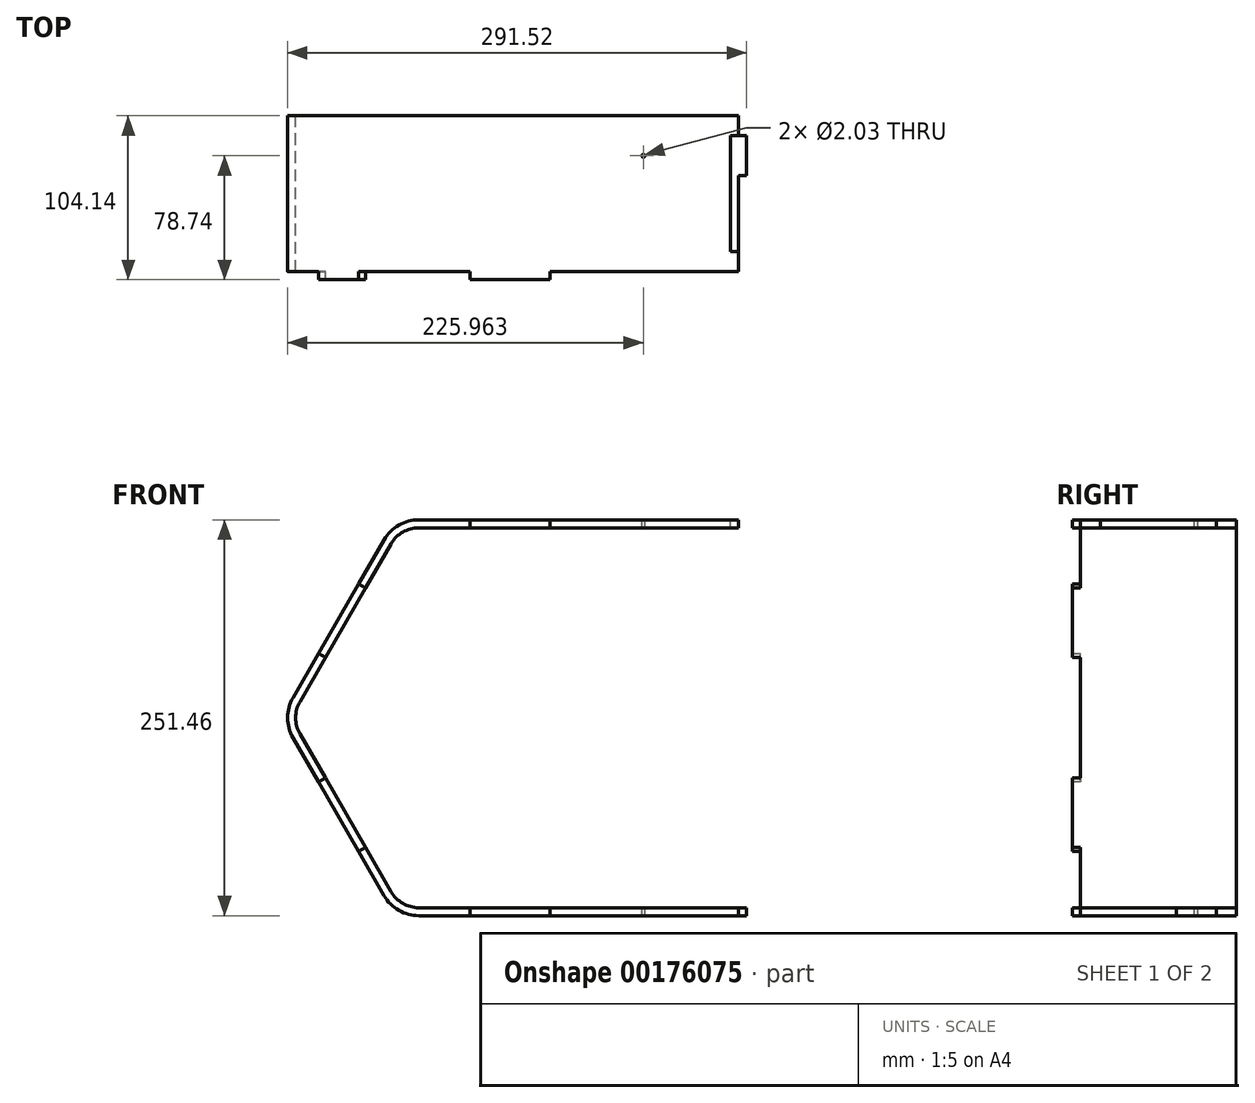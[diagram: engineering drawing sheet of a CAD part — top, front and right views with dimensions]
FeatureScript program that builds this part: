
annotation { "Feature Type Name" : "Feature", "Feature Type Description" : "" }
export const myFeature = defineFeature(function(context is Context, id is Id, definition is map)
    precondition{}
    {
        {
            var Q0;
            Q0=qCreatedBy(makeId("Front.planeOp"),FACE);
            var sketch = newSketch(context, id + "F0", { "sketchPlane" : qUnion([Q0])});
            skLineSegment(sketch, "E0", {"start": v(0, 0) * mm, "end": v(-203.11, 0) * mm});
            skLineSegment(sketch, "E1", {"start": v(-225.11, 12.7) * mm, "end": v(-283.03, 113.03) * mm});
            skLineSegment(sketch, "E2", {"start": v(-283.03, 138.43) * mm, "end": v(-225.11, 238.76) * mm});
            skLineSegment(sketch, "E3", {"start": v(-203.11, 251.46) * mm, "end": v(0, 251.46) * mm});
            skPoint(sketch, "E4.visualSharp", {"position": v(-217.78, 251.46) * mm});
            skArc(sketch, "E4.filletArc", {"start": v(-203.11, 251.46) * mm, "mid": v(-215.81, 248.06) * mm, "end": v(-225.11, 238.76) * mm});
            skPoint(sketch, "E5.visualSharp", {"position": v(-290.37, 125.73) * mm});
            skArc(sketch, "E5.filletArc", {"start": v(-283.03, 138.43) * mm, "mid": v(-286.44, 125.73) * mm, "end": v(-283.03, 113.03) * mm});
            skPoint(sketch, "E6.visualSharp", {"position": v(-217.78, 0) * mm});
            skArc(sketch, "E6.filletArc", {"start": v(-225.11, 12.7) * mm, "mid": v(-215.81, 3.4) * mm, "end": v(-203.11, 0) * mm});
            skLineSegment(sketch, "E7.0", {"start": v(-203.11, 246.38) * mm, "end": v(0, 246.38) * mm});
            skArc(sketch, "E7.1", {"start": v(-203.11, 246.38) * mm, "mid": v(-213.27, 243.66) * mm, "end": v(-220.71, 236.22) * mm});
            skLineSegment(sketch, "E7.2", {"start": v(-278.63, 135.89) * mm, "end": v(-220.71, 236.22) * mm});
            skLineSegment(sketch, "E7.3", {"start": v(0, 5.08) * mm, "end": v(-203.11, 5.08) * mm});
            skArc(sketch, "E7.4", {"start": v(-220.71, 15.24) * mm, "mid": v(-213.27, 7.8) * mm, "end": v(-203.11, 5.08) * mm});
            skLineSegment(sketch, "E7.5", {"start": v(-220.71, 15.24) * mm, "end": v(-278.63, 115.57) * mm});
            skArc(sketch, "E7.6", {"start": v(-278.63, 135.89) * mm, "mid": v(-281.36, 125.73) * mm, "end": v(-278.63, 115.57) * mm});
            skLineSegment(sketch, "E8", {"start": v(0, 246.38) * mm, "end": v(0, 251.46) * mm});
            skLineSegment(sketch, "E9", {"start": v(0, 5.08) * mm, "end": v(0, 0) * mm});
            skSolve(sketch);
        }
        {
            var Q0;
            Q0 = qSketchRegion(id + "F0", true);
            extrude(context, id + "F1", {"entities" : qUnion([Q0]), "depth" : 99.06 * mm});
        }
        {
            var Q0;
            Q0=makeQuery(id+"F1.opExtrude","SWEPT_FACE",FACE,{"disambiguationData":[OSD([sQuery(id+"F0.wireOp",EDGE,"E3")])]});
            var sketch = newSketch(context, id + "F2", { "sketchPlane" : qUnion([Q0])});
            skLineSegment(sketch, "E10.bottom", {"start": v(-170.59, -99.06) * mm, "end": v(-119.79, -99.06) * mm});
            skLineSegment(sketch, "E10.top", {"start": v(-170.59, -104.14) * mm, "end": v(-119.79, -104.14) * mm});
            skLineSegment(sketch, "E10.left", {"start": v(-119.79, -99.06) * mm, "end": v(-119.79, -104.14) * mm});
            skLineSegment(sketch, "E10.right", {"start": v(-170.59, -99.06) * mm, "end": v(-170.59, -104.14) * mm});
            skPoint(sketch, "E11", {"position": v(-145.19, -104.14) * mm});
            skSolve(sketch);
        }
        {
            var Q0;
            Q0=makeQuery(id+"F1.opExtrude","CAP_FACE",FACE,{"disambiguationData":[OSD([sQuery(id+"F0.wireOp",EDGE,"E0"),sQuery(id+"F0.wireOp",EDGE,"E1"),sQuery(id+"F0.wireOp",EDGE,"E2"),sQuery(id+"F0.wireOp",EDGE,"E3"),sQuery(id+"F0.wireOp",EDGE,"E4.filletArc"),sQuery(id+"F0.wireOp",EDGE,"E5.filletArc"),sQuery(id+"F0.wireOp",EDGE,"E6.filletArc"),sQuery(id+"F0.wireOp",EDGE,"E7.0"),sQuery(id+"F0.wireOp",EDGE,"E7.1"),sQuery(id+"F0.wireOp",EDGE,"E7.2"),sQuery(id+"F0.wireOp",EDGE,"E7.3"),sQuery(id+"F0.wireOp",EDGE,"E7.4"),sQuery(id+"F0.wireOp",EDGE,"E7.5"),sQuery(id+"F0.wireOp",EDGE,"E7.6"),sQuery(id+"F0.wireOp",EDGE,"E8"),sQuery(id+"F0.wireOp",EDGE,"E9")])],"isStart":false});
            var Q1;
            Q1=makeQuery(id+"F1.opExtrude","CAP_FACE",FACE,{"disambiguationData":[OSD([sQuery(id+"F0.wireOp",EDGE,"E0"),sQuery(id+"F0.wireOp",EDGE,"E1"),sQuery(id+"F0.wireOp",EDGE,"E2"),sQuery(id+"F0.wireOp",EDGE,"E3"),sQuery(id+"F0.wireOp",EDGE,"E4.filletArc"),sQuery(id+"F0.wireOp",EDGE,"E5.filletArc"),sQuery(id+"F0.wireOp",EDGE,"E6.filletArc"),sQuery(id+"F0.wireOp",EDGE,"E7.0"),sQuery(id+"F0.wireOp",EDGE,"E7.1"),sQuery(id+"F0.wireOp",EDGE,"E7.2"),sQuery(id+"F0.wireOp",EDGE,"E7.3"),sQuery(id+"F0.wireOp",EDGE,"E7.4"),sQuery(id+"F0.wireOp",EDGE,"E7.5"),sQuery(id+"F0.wireOp",EDGE,"E7.6"),sQuery(id+"F0.wireOp",EDGE,"E8"),sQuery(id+"F0.wireOp",EDGE,"E9")])],"isStart":true});
            cPlane(context, id + "F3", {"entities" : qUnion([Q0, Q1]), "cplaneType" : CPlaneType.MID_PLANE, "offset" : 25.4 * mm, "width" : 152.4 * mm, "height" : 152.4 * mm});
        }
        {
            var Q0;
            Q0=makeQuery(id+"F2.imprint","IMPRINT",FACE,{"disambiguationData":[TD([[makeQuery(id+"F2.imprint","IMPRINT",EDGE,{"derivedFrom":sQuery(id+"F2.wireOp",EDGE,"E10.bottom")}),-1.0]])]});
            var Q1;
            Q1=makeQuery(id+"F1.opExtrude","SWEPT_FACE",FACE,{"disambiguationData":[OSD([sQuery(id+"F0.wireOp",EDGE,"E7.0")])]});
            extrude(context, id + "F4", {"entities" : qUnion([Q0]), "operationType" : NewBodyOperationType.ADD, "endBound" : BoundingType.UP_TO_SURFACE, "oppositeDirection" : true, "endBoundEntityFace" : qUnion([Q1]), "depth" : 25.4 * mm});
        }
        {
            var Q0;
            Q0=makeQuery(id+"F1.opExtrude","SWEPT_FACE",FACE,{"disambiguationData":[OSD([sQuery(id+"F0.wireOp",EDGE,"E2")])]});
            var sketch = newSketch(context, id + "F5", { "sketchPlane" : qUnion([Q0])});
            skLineSegment(sketch, "E12.bottom", {"start": v(104.14, 61.7) * mm, "end": v(99.06, 61.7) * mm});
            skLineSegment(sketch, "E12.top", {"start": v(104.14, 10.9) * mm, "end": v(99.06, 10.9) * mm});
            skLineSegment(sketch, "E12.left", {"start": v(104.14, 61.7) * mm, "end": v(104.14, 10.9) * mm});
            skLineSegment(sketch, "E12.right", {"start": v(99.06, 61.7) * mm, "end": v(99.06, 10.9) * mm});
            skPoint(sketch, "E13", {"position": v(99.06, 36.3) * mm});
            skPoint(sketch, "E14", {"position": v(104.14, 36.3) * mm});
            skSolve(sketch);
        }
        {
            var Q0;
            Q0 = qSketchRegion(id + "F5", true);
            var Q1;
            Q1=makeQuery(id+"F1.opExtrude","SWEPT_FACE",FACE,{"disambiguationData":[OSD([sQuery(id+"F0.wireOp",EDGE,"E7.2")])]});
            extrude(context, id + "F6", {"entities" : qUnion([Q0]), "operationType" : NewBodyOperationType.ADD, "endBound" : BoundingType.UP_TO_SURFACE, "oppositeDirection" : true, "endBoundEntityFace" : qUnion([Q1]), "depth" : 25.4 * mm});
        }
        {
            var Q0;
            Q0=makeQuery(id+"F1.opExtrude","SWEPT_FACE",FACE,{"disambiguationData":[OSD([sQuery(id+"F0.wireOp",EDGE,"E1")])]});
            var sketch = newSketch(context, id + "F7", { "sketchPlane" : qUnion([Q0])});
            skPoint(sketch, "E15", {"position": v(99.06, 181.47) * mm});
            skLineSegment(sketch, "E16.bottom", {"start": v(99.06, 206.87) * mm, "end": v(104.14, 206.87) * mm});
            skLineSegment(sketch, "E16.top", {"start": v(99.06, 156.07) * mm, "end": v(104.14, 156.07) * mm});
            skLineSegment(sketch, "E16.left", {"start": v(99.06, 206.87) * mm, "end": v(99.06, 156.07) * mm});
            skLineSegment(sketch, "E16.right", {"start": v(104.14, 206.87) * mm, "end": v(104.14, 156.07) * mm});
            skPoint(sketch, "E17", {"position": v(104.14, 181.47) * mm});
            skSolve(sketch);
        }
        {
            var Q0;
            Q0 = qSketchRegion(id + "F7", true);
            var Q1;
            Q1=makeQuery(id+"F1.opExtrude","SWEPT_FACE",FACE,{"disambiguationData":[OSD([sQuery(id+"F0.wireOp",EDGE,"E7.5")])]});
            extrude(context, id + "F8", {"entities" : qUnion([Q0]), "operationType" : NewBodyOperationType.ADD, "endBound" : BoundingType.UP_TO_SURFACE, "oppositeDirection" : true, "endBoundEntityFace" : qUnion([Q1]), "depth" : 25.4 * mm});
        }
        {
            var Q0;
            Q0=makeQuery(id+"F1.opExtrude","SWEPT_FACE",FACE,{"disambiguationData":[OSD([sQuery(id+"F0.wireOp",EDGE,"E0")])]});
            var sketch = newSketch(context, id + "F9", { "sketchPlane" : qUnion([Q0])});
            skPoint(sketch, "E18", {"position": v(-101.56, 99.06) * mm});
            skLineSegment(sketch, "E19.bottom", {"start": v(-170.59, 99.06) * mm, "end": v(-119.79, 99.06) * mm});
            skLineSegment(sketch, "E19.top", {"start": v(-170.59, 104.14) * mm, "end": v(-119.79, 104.14) * mm});
            skLineSegment(sketch, "E19.left", {"start": v(-170.59, 99.06) * mm, "end": v(-170.59, 104.14) * mm});
            skLineSegment(sketch, "E19.right", {"start": v(-119.79, 99.06) * mm, "end": v(-119.79, 104.14) * mm});
            skPoint(sketch, "E20", {"position": v(-145.19, 104.14) * mm});
            skSolve(sketch);
        }
        {
            var Q0;
            Q0=makeQuery(id+"F9.imprint","IMPRINT",FACE,{"disambiguationData":[TD([[makeQuery(id+"F9.imprint","IMPRINT",EDGE,{"derivedFrom":sQuery(id+"F9.wireOp",EDGE,"E19.bottom")}),-1.0]])]});
            var Q1;
            Q1=makeQuery(id+"F1.opExtrude","SWEPT_FACE",FACE,{"disambiguationData":[OSD([sQuery(id+"F0.wireOp",EDGE,"E7.3")])]});
            extrude(context, id + "F10", {"entities" : qUnion([Q0]), "operationType" : NewBodyOperationType.ADD, "endBound" : BoundingType.UP_TO_SURFACE, "oppositeDirection" : true, "endBoundEntityFace" : qUnion([Q1]), "depth" : 25.4 * mm});
        }
        {
            var Q0;
            {var subQ0=sQuery(id+"F9.wireOp",EDGE,"E19.right");var subQ1=sQuery(id+"F9.wireOp",EDGE,"E19.left");var subQ2=sQuery(id+"F9.wireOp",EDGE,"E19.top");var subQ3=sQuery(id+"F9.wireOp",EDGE,"E19.bottom");Q0=makeQuery(id+"FOcjj00AabnaQMC_1.1.F10.boolean.opBoolean","MERGE",FACE,{"derivedFrom":[makeQuery(id+"F10.boolean.opBoolean","MERGE",FACE,{"derivedFrom":[makeQuery(id+"F1.opExtrude","SWEPT_FACE",FACE,{"disambiguationData":[OSD([sQuery(id+"F0.wireOp",EDGE,"E0")])]}),makeQuery(id+"F10.opExtrude","CAP_FACE",FACE,{"disambiguationData":[OSD([subQ3,subQ2,subQ1,subQ0])],"isStart":true})]}),makeQuery(id+"FOcjj00AabnaQMC_1.1.F10.opExtrude","CAP_FACE",FACE,{"disambiguationData":[OSD([subQ3,subQ2,subQ1,subQ0])],"isStart":true})]});}
            var sketch = newSketch(context, id + "F11", { "sketchPlane" : qUnion([Q0])});
            skLineSegment(sketch, "E21", {"start": v(0, 38.1) * mm, "end": v(5.08, 38.1) * mm});
            skLineSegment(sketch, "E22", {"start": v(5.08, 38.1) * mm, "end": v(5.08, 12.7) * mm});
            skLineSegment(sketch, "E23", {"start": v(5.08, 12.7) * mm, "end": v(0, 12.7) * mm});
            skPoint(sketch, "E24", {"position": v(5.08, 25.4) * mm});
            skSolve(sketch);
        }
        {
            var Q0;
            Q0=makeQuery(id+"F11.imprint","IMPRINT",FACE,{"disambiguationData":[TD([[makeQuery(id+"F11.imprint","IMPRINT",EDGE,{"derivedFrom":sQuery(id+"F11.wireOp",EDGE,"dBCN2MHi-L73X-COiZ-1369-i9UW4HQ0UOL0.bottom")}),-1.0]])]});
            var Q1;
            Q1=makeQuery(id+"F11.imprint","IMPRINT",FACE,{"disambiguationData":[TD([[makeQuery(id+"F11.imprint","IMPRINT",EDGE,{"derivedFrom":sQuery(id+"F11.wireOp",EDGE,"uv0YM2hh-z9AA-CsHQ-nxxI-EjLRfSeFv6UL.bottom")}),1.0]])]});
            var Q2;
            {var subQ0=sQuery(id+"F11.wireOp",EDGE,"E21");Q2=makeQuery(id+"F11.imprint","IMPRINT",FACE,{"disambiguationData":[TD([[makeQuery(id+"F11.imprint","IMPRINT",EDGE,{"derivedFrom":subQ0}),-1.0]])]});}
            var Q3;
            {var subQ0=sQuery(id+"F0.wireOp",EDGE,"E7.3");Q3=makeQuery(id+"FOcjj00AabnaQMC_1.1.F10.boolean.opBoolean","MERGE",FACE,{"derivedFrom":[makeQuery(id+"F10.boolean.opBoolean","MERGE",FACE,{"derivedFrom":[makeQuery(id+"F1.opExtrude","SWEPT_FACE",FACE,{"disambiguationData":[OSD([subQ0])]}),makeQuery(id+"F10.opExtrude","CAP_FACE",FACE,{"disambiguationData":[OSD([subQ0])],"isStart":false})]}),makeQuery(id+"FOcjj00AabnaQMC_1.1.F10.opExtrude","CAP_FACE",FACE,{"disambiguationData":[OSD([subQ0])],"isStart":false})]});}
            extrude(context, id + "F12", {"entities" : qUnion([Q0, Q1, Q2]), "operationType" : NewBodyOperationType.ADD, "endBound" : BoundingType.UP_TO_SURFACE, "oppositeDirection" : true, "endBoundEntityFace" : qUnion([Q3]), "depth" : 25.4 * mm});
        }
        {
            var Q0;
            {var subQ0=sQuery(id+"F2.wireOp",EDGE,"E10.right");var subQ1=sQuery(id+"F2.wireOp",EDGE,"E10.left");var subQ2=sQuery(id+"F2.wireOp",EDGE,"E10.top");var subQ3=sQuery(id+"F2.wireOp",EDGE,"E10.bottom");Q0=makeQuery(id+"FA9yLEBiCmp2qDI_1.1.F4.boolean.opBoolean","MERGE",FACE,{"derivedFrom":[makeQuery(id+"F4.boolean.opBoolean","MERGE",FACE,{"derivedFrom":[makeQuery(id+"F1.opExtrude","SWEPT_FACE",FACE,{"disambiguationData":[OSD([sQuery(id+"F0.wireOp",EDGE,"E3")])]}),makeQuery(id+"F4.opExtrude","CAP_FACE",FACE,{"disambiguationData":[OSD([subQ3,subQ2,subQ1,subQ0])],"isStart":true})]}),makeQuery(id+"FA9yLEBiCmp2qDI_1.1.F4.opExtrude","CAP_FACE",FACE,{"disambiguationData":[OSD([subQ3,subQ2,subQ1,subQ0])],"isStart":true})]});}
            var sketch = newSketch(context, id + "F13", { "sketchPlane" : qUnion([Q0])});
            skLineSegment(sketch, "E25", {"start": v(-5.08, -99.06) * mm, "end": v(-5.08, -86.36) * mm});
            skLineSegment(sketch, "E26", {"start": v(-5.08, -86.36) * mm, "end": v(0, -86.36) * mm});
            skLineSegment(sketch, "E27", {"start": v(0, -12.7) * mm, "end": v(-5.08, -12.7) * mm});
            skLineSegment(sketch, "E28", {"start": v(-5.08, -12.7) * mm, "end": v(-5.08, 0) * mm});
            skLineSegment(sketch, "E29", {"start": v(-5.08, -86.36) * mm, "end": v(-5.08, -12.7) * mm});
            skSolve(sketch);
        }
        {
            var Q0;
            Q0=makeQuery(id+"F13.imprint","IMPRINT",FACE,{"disambiguationData":[TD([[makeQuery(id+"F13.imprint","IMPRINT",EDGE,{"derivedFrom":sQuery(id+"F13.wireOp",EDGE,"I0PWTSSI-DO5l-hUTM-lzc9-wJIb2kJdT08f.bottom")}),1.0]])]});
            var Q1;
            Q1=makeQuery(id+"F13.imprint","IMPRINT",FACE,{"disambiguationData":[TD([[makeQuery(id+"F13.imprint","IMPRINT",EDGE,{"derivedFrom":sQuery(id+"F13.wireOp",EDGE,"Z0djA6Wr-vS1q-zq7I-qstk-N1caMg06y9J0.bottom")}),-1.0]])]});
            var Q2;
            {var subQ0=sQuery(id+"F13.wireOp",EDGE,"E26");Q2=makeQuery(id+"F13.imprint","IMPRINT",FACE,{"disambiguationData":[TD([[makeQuery(id+"F13.imprint","IMPRINT",EDGE,{"derivedFrom":subQ0}),1.0]])]});}
            var Q3;
            {var subQ0=sQuery(id+"F0.wireOp",EDGE,"E7.0");Q3=makeQuery(id+"FA9yLEBiCmp2qDI_1.1.F4.boolean.opBoolean","MERGE",FACE,{"derivedFrom":[makeQuery(id+"F4.boolean.opBoolean","MERGE",FACE,{"derivedFrom":[makeQuery(id+"F1.opExtrude","SWEPT_FACE",FACE,{"disambiguationData":[OSD([subQ0])]}),makeQuery(id+"F4.opExtrude","CAP_FACE",FACE,{"disambiguationData":[OSD([subQ0])],"isStart":false})]}),makeQuery(id+"FA9yLEBiCmp2qDI_1.1.F4.opExtrude","CAP_FACE",FACE,{"disambiguationData":[OSD([subQ0])],"isStart":false})]});}
            extrude(context, id + "F14", {"entities" : qUnion([Q0, Q1, Q2]), "operationType" : NewBodyOperationType.REMOVE, "endBound" : BoundingType.UP_TO_SURFACE, "oppositeDirection" : true, "endBoundEntityFace" : qUnion([Q3]), "depth" : 25.4 * mm});
        }
        {
            var Q0;
            {var subQ0=sQuery(id+"F2.wireOp",EDGE,"E10.right");var subQ1=sQuery(id+"F2.wireOp",EDGE,"E10.left");var subQ2=sQuery(id+"F2.wireOp",EDGE,"E10.top");var subQ3=sQuery(id+"F2.wireOp",EDGE,"E10.bottom");Q0=makeQuery(id+"FA9yLEBiCmp2qDI_1.1.F4.boolean.opBoolean","MERGE",FACE,{"derivedFrom":[makeQuery(id+"F4.boolean.opBoolean","MERGE",FACE,{"derivedFrom":[makeQuery(id+"F1.opExtrude","SWEPT_FACE",FACE,{"disambiguationData":[OSD([sQuery(id+"F0.wireOp",EDGE,"E3")])]}),makeQuery(id+"F4.opExtrude","CAP_FACE",FACE,{"disambiguationData":[OSD([subQ3,subQ2,subQ1,subQ0])],"isStart":true})]}),makeQuery(id+"FA9yLEBiCmp2qDI_1.1.F4.opExtrude","CAP_FACE",FACE,{"disambiguationData":[OSD([subQ3,subQ2,subQ1,subQ0])],"isStart":true})]});}
            var sketch = newSketch(context, id + "F15", { "sketchPlane" : qUnion([Q0])});
            skLineSegment(sketch, "E30.bottom", {"start": v(-63.02, -12.7) * mm, "end": v(-57.94, -12.7) * mm, "construction": true});
            skLineSegment(sketch, "E30.top", {"start": v(-63.02, -38.1) * mm, "end": v(-57.94, -38.1) * mm, "construction": true});
            skLineSegment(sketch, "E30.left", {"start": v(-63.02, -12.7) * mm, "end": v(-63.02, -38.1) * mm, "construction": true});
            skLineSegment(sketch, "E30.right", {"start": v(-57.94, -12.7) * mm, "end": v(-57.94, -38.1) * mm, "construction": true});
            skPoint(sketch, "E31", {"position": v(-63.02, -25.4) * mm});
            skPoint(sketch, "E32", {"position": v(0, -25.4) * mm});
            skPoint(sketch, "E33", {"position": v(-60.48, -12.7) * mm});
            skCircle(sketch, "E34", {"center": v(-60.48, -25.4) * mm, "radius": 1.02 * mm});
            skSolve(sketch);
        }
        {
            var Q0;
            Q0=makeQuery(id+"F15.imprint","IMPRINT",FACE,{"disambiguationData":[TD([[makeQuery(id+"F15.imprint","IMPRINT",EDGE,{"derivedFrom":sQuery(id+"F15.wireOp",EDGE,"E30.bottom")}),-1.0]])]});
            var Q1;
            Q1=makeQuery(id+"F15.imprint","IMPRINT",FACE,{"disambiguationData":[TD([[makeQuery(id+"F15.imprint","IMPRINT",EDGE,{"derivedFrom":sQuery(id+"F15.wireOp",EDGE,"E34")}),1.0]])]});
            extrude(context, id + "F16", {"entities" : qUnion([Q0, Q1]), "operationType" : NewBodyOperationType.REMOVE, "endBound" : BoundingType.THROUGH_ALL, "oppositeDirection" : true, "depth" : 25.4 * mm});
        }
    });
